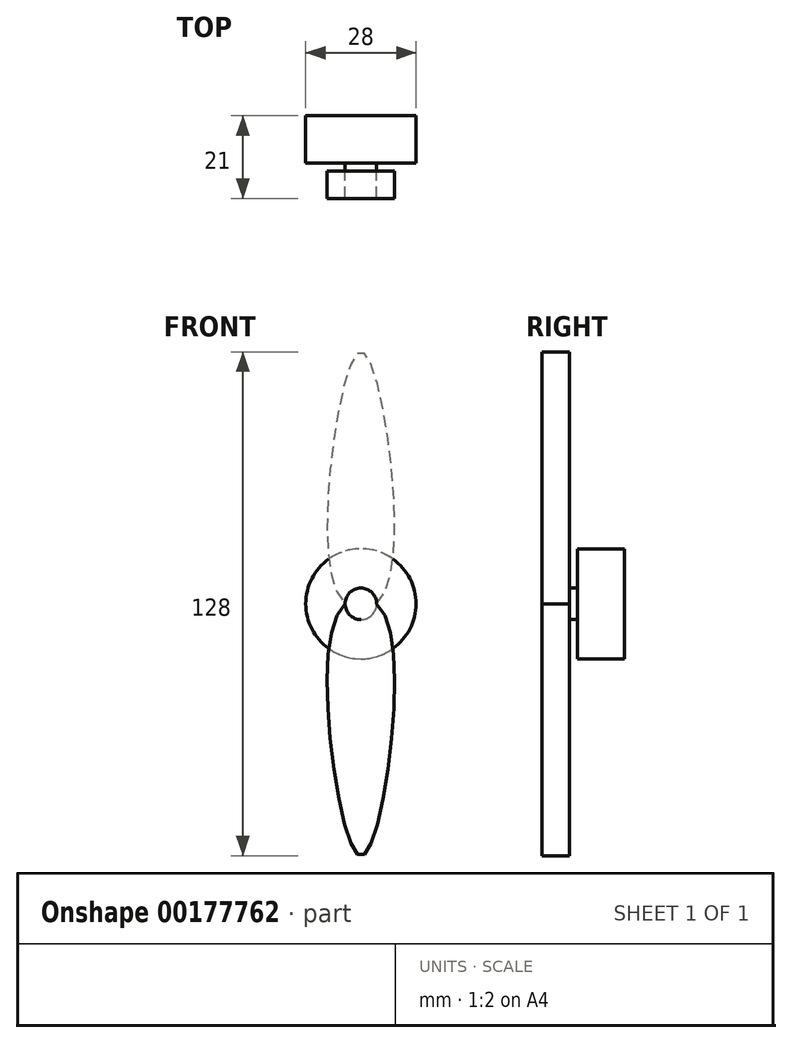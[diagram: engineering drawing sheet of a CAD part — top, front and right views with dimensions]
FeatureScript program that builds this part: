
annotation { "Feature Type Name" : "Feature", "Feature Type Description" : "" }
export const myFeature = defineFeature(function(context is Context, id is Id, definition is map)
    precondition{}
    {
        {
            var Q0;
            Q0=qCreatedBy(makeId("Front.planeOp"),FACE);
            var sketch = newSketch(context, id + "F0", { "sketchPlane" : qUnion([Q0])});
            skCircle(sketch, "E0", {"center": v(0, 0) * mm, "radius": 14 * mm});
            skSolve(sketch);
        }
        {
            var Q0;
            Q0=makeQuery(id+"F0.imprint","IMPRINT",FACE,{"disambiguationData":[TD([[makeQuery(id+"F0.imprint","IMPRINT",EDGE,{"derivedFrom":sQuery(id+"F0.wireOp",EDGE,"E0")}),1.0]])]});
            extrude(context, id + "F1", {"entities" : qUnion([Q0]), "depth" : 12 * mm});
        }
        {
            var Q0;
            Q0=makeQuery(id+"F1.opExtrude","CAP_FACE",FACE,{"disambiguationData":[OSD([sQuery(id+"F0.wireOp",EDGE,"E0")])],"isStart":false});
            var sketch = newSketch(context, id + "F2", { "sketchPlane" : qUnion([Q0])});
            skCircle(sketch, "E1", {"center": v(0, 0) * mm, "radius": 4 * mm});
            skSolve(sketch);
        }
        {
            var Q0;
            Q0=makeQuery(id+"F2.imprint","IMPRINT",FACE,{"disambiguationData":[TD([[makeQuery(id+"F2.imprint","IMPRINT",EDGE,{"derivedFrom":sQuery(id+"F2.wireOp",EDGE,"E1")}),1.0]])]});
            extrude(context, id + "F3", {"entities" : qUnion([Q0]), "operationType" : NewBodyOperationType.ADD, "depth" : 2 * mm});
        }
        {
            var Q0;
            Q0=makeQuery(id+"F3.opExtrude","CAP_FACE",FACE,{"disambiguationData":[OSD([sQuery(id+"F2.wireOp",EDGE,"E1")])],"isStart":false});
            var sketch = newSketch(context, id + "F4", { "sketchPlane" : qUnion([Q0])});
            skPoint(sketch, "E2.middle", {"position": v(0, 32) * mm});
            skFitSpline(sketch, "E3", {"points": [v(0, 64) * mm, v(-8, 32) * mm, v(-4, 0) * mm, v(4, 0) * mm, v(8, 32) * mm, v(0, 64) * mm]});
            skFitSpline(sketch, "E4", {"points": [v(0, -64) * mm, v(-8, -32) * mm, v(-4, 0) * mm, v(4, 0) * mm, v(8, -32) * mm, v(0, -64) * mm]});
            skSolve(sketch);
        }
        {
            var Q0;
            Q0 = qSketchRegion(id + "F4", true);
            extrude(context, id + "F5", {"entities" : qUnion([Q0]), "operationType" : NewBodyOperationType.ADD, "depth" : 7 * mm});
        }
    });
